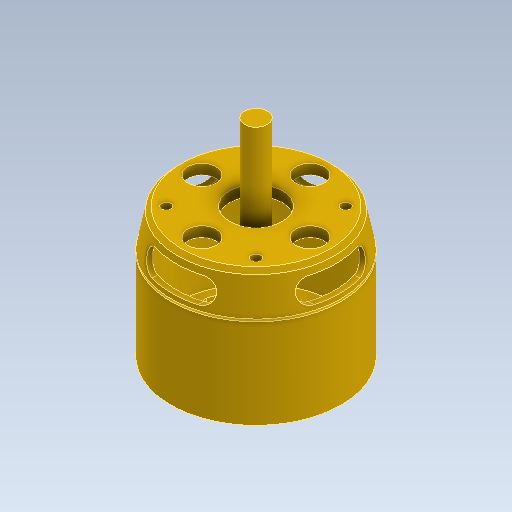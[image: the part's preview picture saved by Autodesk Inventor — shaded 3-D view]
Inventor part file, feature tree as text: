
AUTODESK INVENTOR PART (.ipt)
format: ipt  version: 2023 (Build 270158000, 158)  size: 347,136 bytes
history: native  units: in
note: dims shown in document units (in); Inventor stores cm internally (conversion verified against a paired STEP export)
features: sketch x4, other x3, plane x1
ambient origin geometry x8: Origin, YZ Plane, XZ Plane, XY Plane, X Axis, Y Axis, Z Axis, Center Point
bodies: Solid1 (feature_tree)
feature tree (8):
  other  "Drive Motor.ipt"
  other  "Solid1::Drive Motor.ipt"
  other  "TaggingFeature1"
  sketch  "Sketch1"  dims[d0=0.3937in]
  sketch  "Sketch2"
  sketch  "Sketch3"
  sketch  "Sketch4"
  plane  "Work Plane1"
